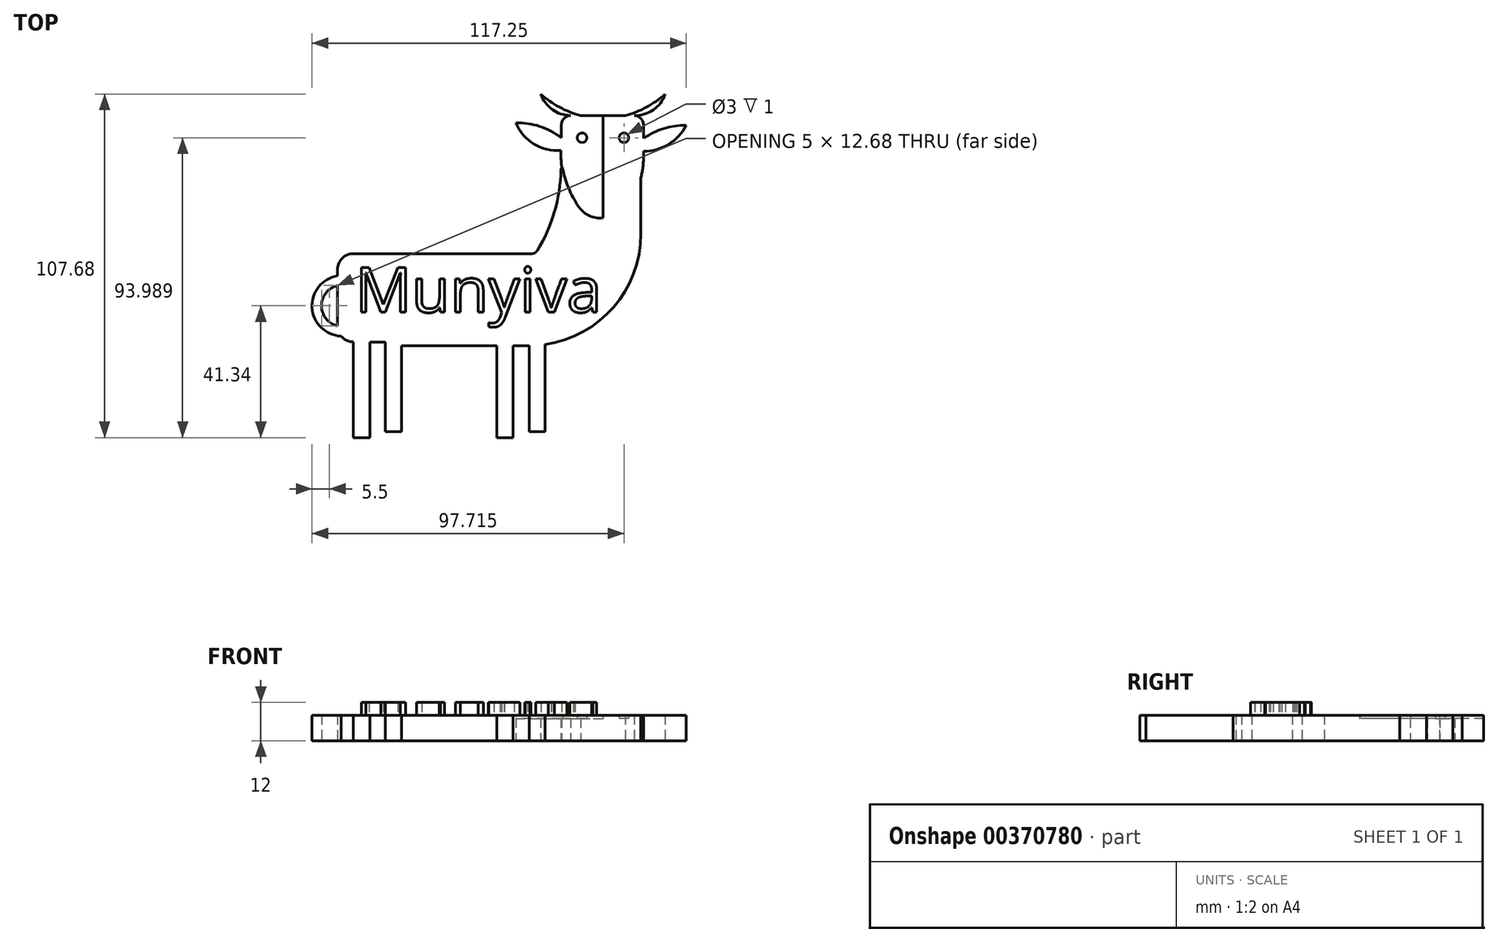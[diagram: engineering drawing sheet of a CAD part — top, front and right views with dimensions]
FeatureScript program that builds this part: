
annotation { "Feature Type Name" : "Feature", "Feature Type Description" : "" }
export const myFeature = defineFeature(function(context is Context, id is Id, definition is map)
    precondition{}
    {
        {
            var Q0;
            Q0=qCreatedBy(makeId("Top.planeOp"),FACE);
            var sketch = newSketch(context, id + "F0", { "sketchPlane" : qUnion([Q0])});
            skLineSegment(sketch, "E0.bottom", {"start": v(-40, 13.84) * mm, "end": v(15.83, 13.84) * mm});
            skLineSegment(sketch, "E0.left", {"start": v(-45, 8.84) * mm, "end": v(-45, -8.84) * mm});
            skPoint(sketch, "E1.visualSharp", {"position": v(-45, -16.16) * mm});
            skArc(sketch, "E1.filletArc", {"start": v(-45, -8.84) * mm, "mid": v(-43.54, -12.37) * mm, "end": v(-40, -13.84) * mm});
            skPoint(sketch, "E2.visualSharp", {"position": v(-45, 13.84) * mm});
            skArc(sketch, "E2.filletArc", {"start": v(-40, 13.84) * mm, "mid": v(-43.54, 12.37) * mm, "end": v(-45, 8.84) * mm});
            skLineSegment(sketch, "E3.right", {"start": v(50, 39.87) * mm, "end": v(50, 20) * mm});
            skArc(sketch, "E4", {"start": v(19.99, -14.64) * mm, "mid": v(41.45, -2.92) * mm, "end": v(50, 20) * mm});
            skArc(sketch, "E5", {"start": v(17.53, 14.79) * mm, "mid": v(22.96, 26.94) * mm, "end": v(25, 40.1) * mm});
            skPoint(sketch, "E6.newPointA", {"position": v(25, 13.84) * mm});
            skArc(sketch, "E6.filletArc", {"start": v(15.83, 13.84) * mm, "mid": v(16.8, 14.1) * mm, "end": v(17.53, 14.79) * mm});
            skPoint(sketch, "E7.visualSharp", {"position": v(25, 41.08) * mm});
            skArc(sketch, "E7.filletArc", {"start": v(25.44, 40.9) * mm, "mid": v(25.11, 40.56) * mm, "end": v(25, 40.1) * mm});
            skLineSegment(sketch, "E8.top", {"start": v(-40, -43.84) * mm, "end": v(-34.9, -43.84) * mm});
            skLineSegment(sketch, "E8.left", {"start": v(-40, -13.84) * mm, "end": v(-40, -43.84) * mm});
            skLineSegment(sketch, "E8.right", {"start": v(-34.9, -13.84) * mm, "end": v(-34.9, -43.84) * mm});
            skLineSegment(sketch, "E9.top", {"start": v(-30, -42) * mm, "end": v(-25, -42) * mm});
            skLineSegment(sketch, "E9.left", {"start": v(-30, -13.84) * mm, "end": v(-30, -42) * mm});
            skLineSegment(sketch, "E9.right", {"start": v(-25, -15) * mm, "end": v(-25, -42) * mm});
            skLineSegment(sketch, "E10.left", {"start": v(4.9, -15) * mm, "end": v(4.9, -43.84) * mm});
            skLineSegment(sketch, "E10.right", {"start": v(10, -15) * mm, "end": v(10, -43.84) * mm});
            skLineSegment(sketch, "E11.left", {"start": v(15, -15) * mm, "end": v(15, -42) * mm});
            skLineSegment(sketch, "E11.right", {"start": v(19.99, -14.64) * mm, "end": v(19.99, -42) * mm});
            skLineSegment(sketch, "E12.left", {"start": v(-40, -41.74) * mm, "end": v(-40, -43.84) * mm});
            skLineSegment(sketch, "E12.right", {"start": v(-34.9, -41.74) * mm, "end": v(-34.9, -43.84) * mm});
            skLineSegment(sketch, "E13.left", {"start": v(-30, -40) * mm, "end": v(-30, -42) * mm});
            skLineSegment(sketch, "E13.right", {"start": v(-25, -40) * mm, "end": v(-25, -42) * mm});
            skLineSegment(sketch, "E14.top", {"start": v(15, -42) * mm, "end": v(19.99, -42) * mm});
            skLineSegment(sketch, "E14.left", {"start": v(15, -40) * mm, "end": v(15, -42) * mm});
            skLineSegment(sketch, "E14.right", {"start": v(19.99, -40) * mm, "end": v(19.99, -42) * mm});
            skLineSegment(sketch, "E15.top", {"start": v(4.9, -43.84) * mm, "end": v(10, -43.84) * mm});
            skLineSegment(sketch, "E15.left", {"start": v(4.9, -41.74) * mm, "end": v(4.9, -43.84) * mm});
            skLineSegment(sketch, "E15.right", {"start": v(10, -42.9) * mm, "end": v(10, -43.84) * mm});
            skArc(sketch, "E16", {"start": v(24.87, 48.05) * mm, "mid": v(26.18, 37.83) * mm, "end": v(30.57, 28.5) * mm});
            skArc(sketch, "E17", {"start": v(42.72, 27.23) * mm, "mid": v(48.65, 35.8) * mm, "end": v(50.73, 46) * mm});
            skArc(sketch, "E18", {"start": v(30.57, 28.5) * mm, "mid": v(36.35, 25.04) * mm, "end": v(42.72, 27.23) * mm});
            skArc(sketch, "E19.filletArc", {"start": v(27.9, 59) * mm, "mid": v(25.83, 58.08) * mm, "end": v(25, 55.97) * mm});
            skArc(sketch, "E20.filletArc", {"start": v(50.73, 56) * mm, "mid": v(49.85, 58.12) * mm, "end": v(47.73, 59) * mm});
            skPoint(sketch, "E21.start.orphan", {"position": v(-45, 3.84) * mm});
            skPoint(sketch, "E22.end.orphan", {"position": v(-35, -5) * mm});
            skPoint(sketch, "E22.start.orphan", {"position": v(-45, -1.16) * mm});
            skArc(sketch, "E23", {"start": v(-45, 3.76) * mm, "mid": v(-45, 3.8) * mm, "end": v(-45, 3.84) * mm});
            skLineSegment(sketch, "E24", {"start": v(50.73, 56) * mm, "end": v(50.73, 51.85) * mm});
            skArc(sketch, "E25", {"start": v(10.73, 56.67) * mm, "mid": v(16.4, 50.05) * mm, "end": v(24.87, 48.05) * mm});
            skArc(sketch, "E26", {"start": v(24.93, 52.01) * mm, "mid": v(18.24, 55.58) * mm, "end": v(10.73, 56.67) * mm});
            skArc(sketch, "E27", {"start": v(50.73, 47.74) * mm, "mid": v(58.6, 49.96) * mm, "end": v(64.13, 55.97) * mm});
            skArc(sketch, "E28", {"start": v(64.13, 55.97) * mm, "mid": v(57.12, 54.92) * mm, "end": v(50.73, 51.85) * mm});
            skArc(sketch, "E29", {"start": v(18.55, 65.7) * mm, "mid": v(22.17, 60.87) * mm, "end": v(27.9, 59) * mm});
            skArc(sketch, "E30", {"start": v(18.55, 65.7) * mm, "mid": v(24.4, 61.6) * mm, "end": v(31.05, 59) * mm});
            skPoint(sketch, "E31.orphan", {"position": v(-51.92, -8.84) * mm});
            skArc(sketch, "E32", {"start": v(-45, 3.84) * mm, "mid": v(-50, -2.5) * mm, "end": v(-45, -8.84) * mm});
            skArc(sketch, "E33.0", {"start": v(-43.48, 7.02) * mm, "mid": v(-53, -2.5) * mm, "end": v(-43.48, -12.02) * mm});
            skLineSegment(sketch, "E34.trimOffspring", {"start": v(50.73, 47.74) * mm, "end": v(50.73, 46) * mm});
            skArc(sketch, "E35.MirrorCS", {"start": v(57.52, 65.7) * mm, "mid": v(53.73, 60.74) * mm, "end": v(47.73, 59) * mm});
            skArc(sketch, "E36.MirrorCS", {"start": v(57.52, 65.7) * mm, "mid": v(51.67, 61.6) * mm, "end": v(45.02, 59) * mm});
            skLineSegment(sketch, "E37.trimOffspring", {"start": v(10, -15) * mm, "end": v(15, -15) * mm});
            skLineSegment(sketch, "E38.trimOffspring", {"start": v(-25, -15) * mm, "end": v(4.9, -15) * mm});
            skLineSegment(sketch, "E39", {"start": v(-30, -13.84) * mm, "end": v(-34.9, -13.84) * mm});
            skLineSegment(sketch, "E40", {"start": v(31.05, 59) * mm, "end": v(45.02, 59) * mm});
            skLineSegment(sketch, "E41", {"start": v(24.93, 52.01) * mm, "end": v(25, 55.97) * mm});
            skSolve(sketch);
        }
        {
            var Q0;
            {var subQ0=sQuery(id+"F0.wireOp",EDGE,"E32");Q0=makeQuery(id+"F0.imprint","IMPRINT",FACE,{"disambiguationData":[TD([[makeQuery(id+"F0.imprint","IMPRINT",EDGE,{"derivedFrom":subQ0}),-1.0]])]});}
            var Q1;
            Q1=makeQuery(id+"F0.imprint","IMPRINT",FACE,{"disambiguationData":[TD([[makeQuery(id+"F0.imprint","IMPRINT",EDGE,{"derivedFrom":sQuery(id+"F0.wireOp",EDGE,"E0.bottom")}),-1.0]])]});
            extrude(context, id + "F1", {"entities" : qUnion([Q0, Q1]), "depth" : 8 * mm});
        }
        {
            var Q0;
            Q0=qCreatedBy(makeId("Top.planeOp"),FACE);
            var sketch = newSketch(context, id + "F2", { "sketchPlane" : qUnion([Q0])});
            skArc(sketch, "E42", {"start": v(24.99, 46.19) * mm, "mid": v(26.3, 35.96) * mm, "end": v(30.69, 26.64) * mm});
            skArc(sketch, "E43", {"start": v(42.84, 25.36) * mm, "mid": v(48.76, 33.93) * mm, "end": v(50.85, 44.13) * mm});
            skArc(sketch, "E44", {"start": v(30.69, 26.64) * mm, "mid": v(36.47, 23.18) * mm, "end": v(42.84, 25.36) * mm});
            skArc(sketch, "E45.filletArc", {"start": v(28.02, 57.14) * mm, "mid": v(25.95, 56.22) * mm, "end": v(25.1, 54.11) * mm});
            skArc(sketch, "E46.filletArc", {"start": v(50.85, 54.14) * mm, "mid": v(49.97, 56.26) * mm, "end": v(47.85, 57.14) * mm});
            skLineSegment(sketch, "E47", {"start": v(50.85, 54.14) * mm, "end": v(50.85, 50) * mm});
            skArc(sketch, "E48", {"start": v(10.85, 54.8) * mm, "mid": v(16.5, 48.18) * mm, "end": v(24.99, 46.19) * mm});
            skArc(sketch, "E49", {"start": v(25.05, 50.15) * mm, "mid": v(18.36, 53.72) * mm, "end": v(10.85, 54.8) * mm});
            skArc(sketch, "E50", {"start": v(50.85, 45.87) * mm, "mid": v(58.71, 48.1) * mm, "end": v(64.25, 54.1) * mm});
            skArc(sketch, "E51", {"start": v(64.25, 54.1) * mm, "mid": v(57.24, 53.06) * mm, "end": v(50.85, 50) * mm});
            skArc(sketch, "E52", {"start": v(18.67, 63.84) * mm, "mid": v(22.28, 59) * mm, "end": v(28.02, 57.14) * mm});
            skArc(sketch, "E53", {"start": v(18.67, 63.84) * mm, "mid": v(24.52, 59.74) * mm, "end": v(31.17, 57.14) * mm});
            skLineSegment(sketch, "E54.trimOffspring", {"start": v(50.85, 45.87) * mm, "end": v(50.85, 44.13) * mm});
            skArc(sketch, "E55.MirrorCS", {"start": v(57.64, 63.84) * mm, "mid": v(53.84, 58.88) * mm, "end": v(47.85, 57.14) * mm});
            skArc(sketch, "E56.MirrorCS", {"start": v(57.64, 63.84) * mm, "mid": v(51.79, 59.74) * mm, "end": v(45.13, 57.14) * mm});
            skLineSegment(sketch, "E57", {"start": v(31.17, 57.14) * mm, "end": v(45.13, 57.14) * mm});
            skLineSegment(sketch, "E58", {"start": v(25.05, 50.15) * mm, "end": v(25.1, 54.11) * mm});
            skSolve(sketch);
        }
        {
            var Q0;
            Q0 = qSketchRegion(id + "F2", true);
            extrude(context, id + "F3", {"entities" : qUnion([Q0]), "operationType" : NewBodyOperationType.ADD, "depth" : 7 * mm});
        }
        {
            var Q0;
            Q0=makeQuery(id+"F1.opExtrude","CAP_FACE",FACE,{"disambiguationData":[OSD([sQuery(id+"F0.wireOp",EDGE,"E0.bottom"),sQuery(id+"F0.wireOp",EDGE,"E0.left"),sQuery(id+"F0.wireOp",EDGE,"E1.filletArc"),sQuery(id+"F0.wireOp",EDGE,"E2.filletArc"),sQuery(id+"F0.wireOp",EDGE,"E3.right"),sQuery(id+"F0.wireOp",EDGE,"E4"),sQuery(id+"F0.wireOp",EDGE,"E5"),sQuery(id+"F0.wireOp",EDGE,"E6.filletArc"),sQuery(id+"F0.wireOp",EDGE,"E7.filletArc"),sQuery(id+"F0.wireOp",EDGE,"E8.left"),sQuery(id+"F0.wireOp",EDGE,"E8.right"),sQuery(id+"F0.wireOp",EDGE,"E9.left"),sQuery(id+"F0.wireOp",EDGE,"E9.right"),sQuery(id+"F0.wireOp",EDGE,"E10.left"),sQuery(id+"F0.wireOp",EDGE,"E10.right"),sQuery(id+"F0.wireOp",EDGE,"E11.left"),sQuery(id+"F0.wireOp",EDGE,"E11.right"),sQuery(id+"F0.wireOp",EDGE,"E8.top"),sQuery(id+"F0.wireOp",EDGE,"E12.left"),sQuery(id+"F0.wireOp",EDGE,"E12.right"),sQuery(id+"F0.wireOp",EDGE,"E9.top"),sQuery(id+"F0.wireOp",EDGE,"E13.left"),sQuery(id+"F0.wireOp",EDGE,"E13.right"),sQuery(id+"F0.wireOp",EDGE,"E14.top"),sQuery(id+"F0.wireOp",EDGE,"E14.left"),sQuery(id+"F0.wireOp",EDGE,"E14.right"),sQuery(id+"F0.wireOp",EDGE,"E15.top"),sQuery(id+"F0.wireOp",EDGE,"E15.left"),sQuery(id+"F0.wireOp",EDGE,"E15.right"),sQuery(id+"F0.wireOp",EDGE,"E16"),sQuery(id+"F0.wireOp",EDGE,"E17"),sQuery(id+"F0.wireOp",EDGE,"E18"),sQuery(id+"F0.wireOp",EDGE,"E23"),sQuery(id+"F0.wireOp",EDGE,"E32"),sQuery(id+"F0.wireOp",EDGE,"E33.0"),sQuery(id+"F0.wireOp",EDGE,"E37.trimOffspring"),sQuery(id+"F0.wireOp",EDGE,"E38.trimOffspring"),sQuery(id+"F0.wireOp",EDGE,"E39")])],"isStart":false});
            var sketch = newSketch(context, id + "F4", { "sketchPlane" : qUnion([Q0])});
            skPoint(sketch, "E59.firstSnap0", {"position": v(-25, -28.5) * mm});
            skText(sketch, "E60", { "text": "Munyiva", "fontName": "OpenSans-Regular.ttf"});
            const initialGuessF4  = {"E60": [-0.03949, -0.00454, 1, 0, 0.0141]};
            skSetInitialGuess(sketch, initialGuessF4);
            skSolve(sketch);
        }
        {
            var Q0;
            Q0=makeQuery(id+"F3.opExtrude","CAP_FACE",FACE,{"disambiguationData":[OSD([sQuery(id+"F2.wireOp",EDGE,"E42"),sQuery(id+"F2.wireOp",EDGE,"E43"),sQuery(id+"F2.wireOp",EDGE,"E44"),sQuery(id+"F2.wireOp",EDGE,"E45.filletArc"),sQuery(id+"F2.wireOp",EDGE,"E46.filletArc"),sQuery(id+"F2.wireOp",EDGE,"E47"),sQuery(id+"F2.wireOp",EDGE,"E48"),sQuery(id+"F2.wireOp",EDGE,"E49"),sQuery(id+"F2.wireOp",EDGE,"E50"),sQuery(id+"F2.wireOp",EDGE,"E51"),sQuery(id+"F2.wireOp",EDGE,"E52"),sQuery(id+"F2.wireOp",EDGE,"E53"),sQuery(id+"F2.wireOp",EDGE,"E54.trimOffspring"),sQuery(id+"F2.wireOp",EDGE,"E55.MirrorCS"),sQuery(id+"F2.wireOp",EDGE,"E56.MirrorCS"),sQuery(id+"F2.wireOp",EDGE,"E57"),sQuery(id+"F2.wireOp",EDGE,"E58")])],"isStart":false});
            var sketch = newSketch(context, id + "F5", { "sketchPlane" : qUnion([Q0])});
            skCircle(sketch, "E61", {"center": v(31.6, 50.15) * mm, "radius": 1.5 * mm});
            skLineSegment(sketch, "E62", {"start": v(38.15, 57.14) * mm, "end": v(38.15, 25.06) * mm});
            skCircle(sketch, "E63.MirrorC", {"center": v(44.72, 50.15) * mm, "radius": 1.5 * mm});
            skSolve(sketch);
        }
        {
            var Q0;
            Q0=makeQuery(id+"F5.imprint","IMPRINT",FACE,{"disambiguationData":[TD([[makeQuery(id+"F5.imprint","IMPRINT",EDGE,{"derivedFrom":sQuery(id+"F5.wireOp",EDGE,"E61")}),1.0]])]});
            var Q1;
            Q1=makeQuery(id+"F5.imprint","IMPRINT",FACE,{"disambiguationData":[TD([[makeQuery(id+"F5.imprint","IMPRINT",EDGE,{"derivedFrom":sQuery(id+"F5.wireOp",EDGE,"E63.MirrorC")}),-1.0]])]});
            extrude(context, id + "F6", {"entities" : qUnion([Q0, Q1]), "operationType" : NewBodyOperationType.ADD, "depth" : 1 * mm});
        }
        {
            var Q0;
            Q0=makeQuery(id+"F4.imprint","IMPRINT",FACE,{"disambiguationData":[TD([[makeQuery(id+"F4.imprint","IMPRINT",EDGE,{"derivedFrom":sQuery(id+"F4.wireOp",EDGE,"E60.sketch_text.stroke-0")}),-1.0]])]});
            var Q1;
            Q1=makeQuery(id+"F4.imprint","IMPRINT",FACE,{"disambiguationData":[TD([[makeQuery(id+"F4.imprint","IMPRINT",EDGE,{"derivedFrom":sQuery(id+"F4.wireOp",EDGE,"E60.sketch_text.stroke-18")}),-1.0]])]});
            var Q2;
            Q2=makeQuery(id+"F4.imprint","IMPRINT",FACE,{"disambiguationData":[TD([[makeQuery(id+"F4.imprint","IMPRINT",EDGE,{"derivedFrom":sQuery(id+"F4.wireOp",EDGE,"E60.sketch_text.stroke-35")}),-1.0]])]});
            var Q3;
            Q3=makeQuery(id+"F4.imprint","IMPRINT",FACE,{"disambiguationData":[TD([[makeQuery(id+"F4.imprint","IMPRINT",EDGE,{"derivedFrom":sQuery(id+"F4.wireOp",EDGE,"E60.sketch_text.stroke-52")}),-1.0]])]});
            var Q4;
            Q4=makeQuery(id+"F4.imprint","IMPRINT",FACE,{"disambiguationData":[TD([[makeQuery(id+"F4.imprint","IMPRINT",EDGE,{"derivedFrom":sQuery(id+"F4.wireOp",EDGE,"E60.sketch_text.stroke-68")}),-1.0]])]});
            var Q5;
            Q5=makeQuery(id+"F4.imprint","IMPRINT",FACE,{"disambiguationData":[TD([[makeQuery(id+"F4.imprint","IMPRINT",EDGE,{"derivedFrom":sQuery(id+"F4.wireOp",EDGE,"E60.sketch_text.stroke-80")}),-1.0]])]});
            var Q6;
            Q6=makeQuery(id+"F4.imprint","IMPRINT",FACE,{"disambiguationData":[TD([[makeQuery(id+"F4.imprint","IMPRINT",EDGE,{"derivedFrom":sQuery(id+"F4.wireOp",EDGE,"E60.sketch_text.stroke-72")}),-1.0]])]});
            var Q7;
            Q7=makeQuery(id+"F4.imprint","IMPRINT",FACE,{"disambiguationData":[TD([[makeQuery(id+"F4.imprint","IMPRINT",EDGE,{"derivedFrom":sQuery(id+"F4.wireOp",EDGE,"E60.sketch_text.stroke-90")}),-1.0]])]});
            extrude(context, id + "F7", {"entities" : qUnion([Q0, Q1, Q2, Q3, Q4, Q5, Q6, Q7]), "operationType" : NewBodyOperationType.ADD, "depth" : 4 * mm});
        }
    });
